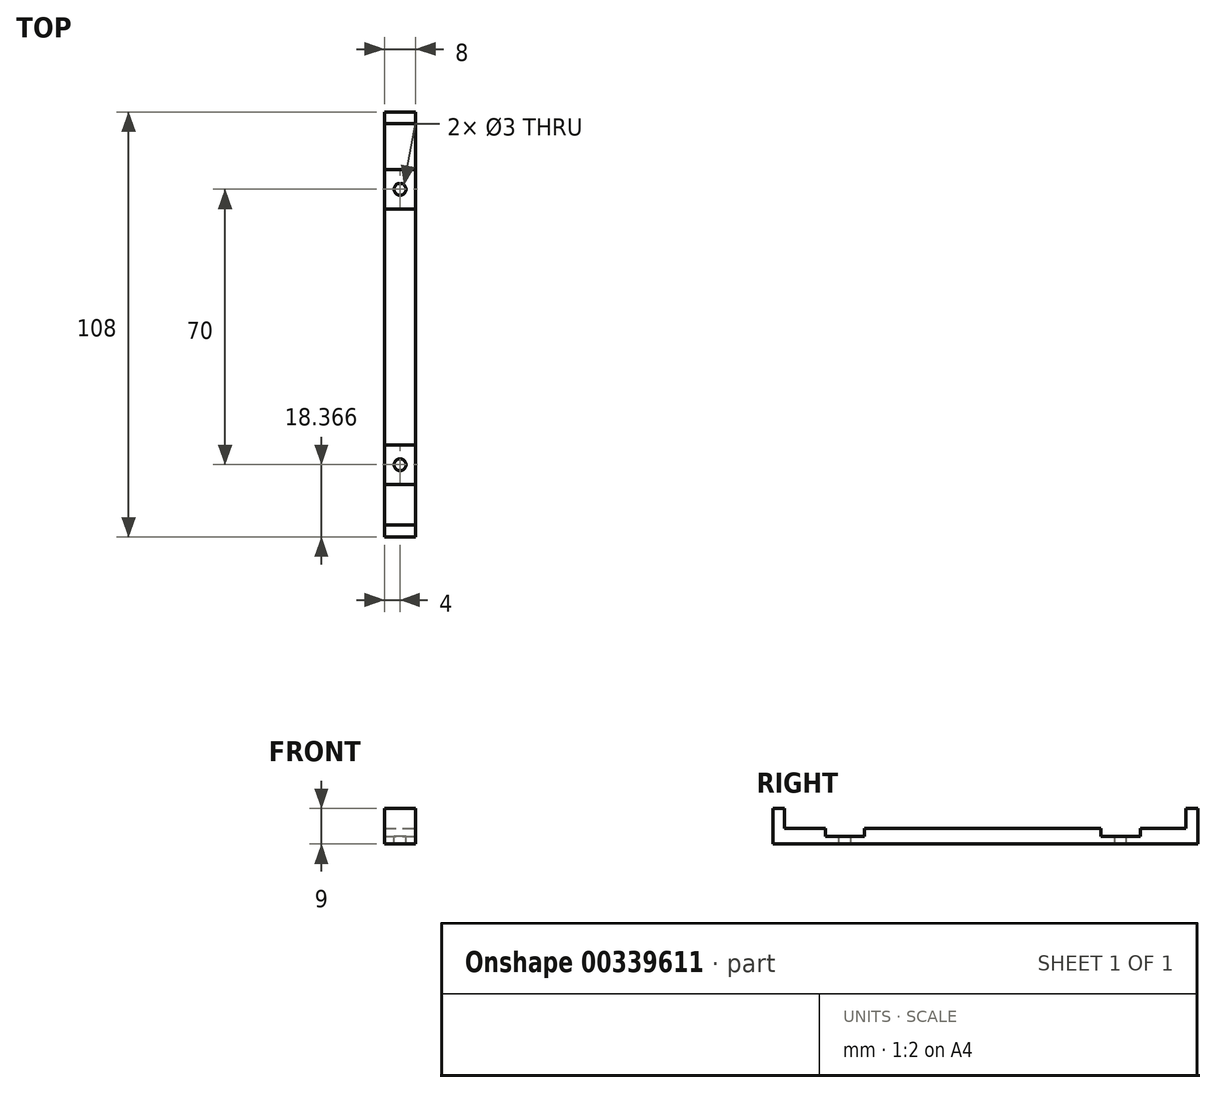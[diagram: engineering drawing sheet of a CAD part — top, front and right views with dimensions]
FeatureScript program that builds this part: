
annotation { "Feature Type Name" : "Feature", "Feature Type Description" : "" }
export const myFeature = defineFeature(function(context is Context, id is Id, definition is map)
    precondition{}
    {
        {
            var Q0;
            Q0=qCreatedBy(makeId("Top.planeOp"),FACE);
            var sketch = newSketch(context, id + "F0", { "sketchPlane" : qUnion([Q0])});
            skLineSegment(sketch, "E0.bottom", {"start": v(-4, 54) * mm, "end": v(4, 54) * mm});
            skLineSegment(sketch, "E0.top", {"start": v(-4, -54) * mm, "end": v(4, -54) * mm});
            skLineSegment(sketch, "E0.left", {"start": v(-4, 54) * mm, "end": v(-4, -54) * mm});
            skLineSegment(sketch, "E0.right", {"start": v(4, 54) * mm, "end": v(4, -54) * mm});
            skLineSegment(sketch, "E1", {"start": v(-4, 54) * mm, "end": v(4, -54) * mm, "construction": true});
            skPoint(sketch, "E2", {"position": v(0, 0) * mm});
            skSolve(sketch);
        }
        {
            var Q0;
            Q0=qSketchRegion(id+"F0",true);
            var Q1;
            Q1=makeQuery(id+"F0.imprint","IMPRINT",FACE,{"disambiguationData":[TD([[makeQuery(id+"F0.imprint","IMPRINT",EDGE,{"derivedFrom":sQuery(id+"F0.wireOp",EDGE,"E0.bottom")}),-1.0]])]});
            extrude(context, id + "F1", {"entities" : qUnion([Q0, Q1]), "endBound" : BoundingType.SYMMETRIC, "depth" : 4 * mm});
        }
        {
            var Q0;
            Q0=makeQuery(id+"F1.opExtrude","CAP_FACE",FACE,{"disambiguationData":[OSD([sQuery(id+"F0.wireOp",EDGE,"E0.bottom"),sQuery(id+"F0.wireOp",EDGE,"E0.top"),sQuery(id+"F0.wireOp",EDGE,"E0.left"),sQuery(id+"F0.wireOp",EDGE,"E0.right")])],"isStart":false});
            var sketch = newSketch(context, id + "F2", { "sketchPlane" : qUnion([Q0])});
            skLineSegment(sketch, "E3.bottom", {"start": v(-4, 54) * mm, "end": v(4, 54) * mm});
            skLineSegment(sketch, "E3.top", {"start": v(-4, 51) * mm, "end": v(4, 51) * mm});
            skLineSegment(sketch, "E3.left", {"start": v(-4, 54) * mm, "end": v(-4, 51) * mm});
            skLineSegment(sketch, "E3.right", {"start": v(4, 54) * mm, "end": v(4, 51) * mm});
            skLineSegment(sketch, "E4.bottom", {"start": v(-4, -54) * mm, "end": v(4, -54) * mm});
            skLineSegment(sketch, "E4.top", {"start": v(-4, -51) * mm, "end": v(4, -51) * mm});
            skLineSegment(sketch, "E4.left", {"start": v(-4, -54) * mm, "end": v(-4, -51) * mm});
            skLineSegment(sketch, "E4.right", {"start": v(4, -54) * mm, "end": v(4, -51) * mm});
            skSolve(sketch);
        }
        {
            var Q0;
            Q0=makeQuery(id+"F2.imprint","IMPRINT",FACE,{"disambiguationData":[TD([[makeQuery(id+"F2.imprint","IMPRINT",EDGE,{"derivedFrom":sQuery(id+"F2.wireOp",EDGE,"E3.bottom")}),-1.0]])]});
            var Q1;
            Q1=makeQuery(id+"F2.imprint","IMPRINT",FACE,{"disambiguationData":[TD([[makeQuery(id+"F2.imprint","IMPRINT",EDGE,{"derivedFrom":sQuery(id+"F2.wireOp",EDGE,"E4.bottom")}),1.0]])]});
            extrude(context, id + "F3", {"entities" : qUnion([Q0, Q1]), "operationType" : NewBodyOperationType.ADD, "depth" : 5 * mm});
        }
        {
            var Q0;
            Q0=makeQuery(id+"F1.opExtrude","CAP_FACE",FACE,{"disambiguationData":[OSD([sQuery(id+"F0.wireOp",EDGE,"E0.bottom"),sQuery(id+"F0.wireOp",EDGE,"E0.top"),sQuery(id+"F0.wireOp",EDGE,"E0.left"),sQuery(id+"F0.wireOp",EDGE,"E0.right")])],"isStart":false});
            var sketch = newSketch(context, id + "F4", { "sketchPlane" : qUnion([Q0])});
            skLineSegment(sketch, "E5", {"start": v(0, 34.37) * mm, "end": v(0, -35.63) * mm});
            skPoint(sketch, "E6", {"position": v(0, 0) * mm});
            skSolve(sketch);
        }
        {
            var Q0;
            Q0=sQuery(id+"F4.wireOp",VERTEX,"E5.start");
            var Q1;
            Q1=sQuery(id+"F4.wireOp",VERTEX,"E5.end");
            var Q2;
            Q2=makeQuery(id+"F1.opExtrude","SWEPT_BODY",BODY,{"disambiguationData":[OSD([sQuery(id+"F0.wireOp",EDGE,"E0.bottom"),sQuery(id+"F0.wireOp",EDGE,"E0.top"),sQuery(id+"F0.wireOp",EDGE,"E0.left"),sQuery(id+"F0.wireOp",EDGE,"E0.right")])]});
            hole(context, id + "F5", {"style" : HoleStyle.SIMPLE, "holeDiameter" : 3 * mm, "endStyle" : HoleEndStyle.THROUGH, "locations" : qUnion([Q0, Q1]), "scope" : qUnion([Q2])});
        }
        {
            var Q0;
            Q0=makeQuery(id+"F1.opExtrude","CAP_FACE",FACE,{"disambiguationData":[OSD([sQuery(id+"F0.wireOp",EDGE,"E0.bottom"),sQuery(id+"F0.wireOp",EDGE,"E0.top"),sQuery(id+"F0.wireOp",EDGE,"E0.left"),sQuery(id+"F0.wireOp",EDGE,"E0.right")])],"isStart":false});
            var sketch = newSketch(context, id + "F6", { "sketchPlane" : qUnion([Q0])});
            skLineSegment(sketch, "E7.bottom", {"start": v(-4, 39.37) * mm, "end": v(4, 39.37) * mm});
            skLineSegment(sketch, "E7.top", {"start": v(-4, 29.37) * mm, "end": v(4, 29.37) * mm});
            skLineSegment(sketch, "E7.left", {"start": v(-4, 39.37) * mm, "end": v(-4, 29.37) * mm});
            skLineSegment(sketch, "E7.right", {"start": v(4, 39.37) * mm, "end": v(4, 29.37) * mm});
            skLineSegment(sketch, "E8.bottom", {"start": v(-4, -40.63) * mm, "end": v(4, -40.63) * mm});
            skLineSegment(sketch, "E8.top", {"start": v(-4, -30.63) * mm, "end": v(4, -30.63) * mm});
            skLineSegment(sketch, "E8.left", {"start": v(-4, -40.63) * mm, "end": v(-4, -30.63) * mm});
            skLineSegment(sketch, "E8.right", {"start": v(4, -40.63) * mm, "end": v(4, -30.63) * mm});
            skLineSegment(sketch, "E9", {"start": v(-4, 39.37) * mm, "end": v(4, 29.37) * mm, "construction": true});
            skLineSegment(sketch, "E10", {"start": v(-4, -30.63) * mm, "end": v(4, -40.63) * mm, "construction": true});
            skPoint(sketch, "E11", {"position": v(0, -35.63) * mm});
            skPoint(sketch, "E12", {"position": v(0, 34.37) * mm});
            skSolve(sketch);
        }
        {
            var Q0;
            Q0=makeQuery(id+"F6.imprint","IMPRINT",FACE,{"disambiguationData":[TD([[makeQuery(id+"F6.imprint","IMPRINT",EDGE,{"derivedFrom":sQuery(id+"F6.wireOp",EDGE,"E8.bottom")}),1.0]])]});
            var Q1;
            Q1=makeQuery(id+"F6.imprint","IMPRINT",FACE,{"disambiguationData":[TD([[makeQuery(id+"F6.imprint","IMPRINT",EDGE,{"derivedFrom":sQuery(id+"F6.wireOp",EDGE,"E7.bottom")}),-1.0]])]});
            extrude(context, id + "F7", {"entities" : qUnion([Q0, Q1]), "operationType" : NewBodyOperationType.REMOVE, "oppositeDirection" : true, "depth" : 2 * mm});
        }
    });
